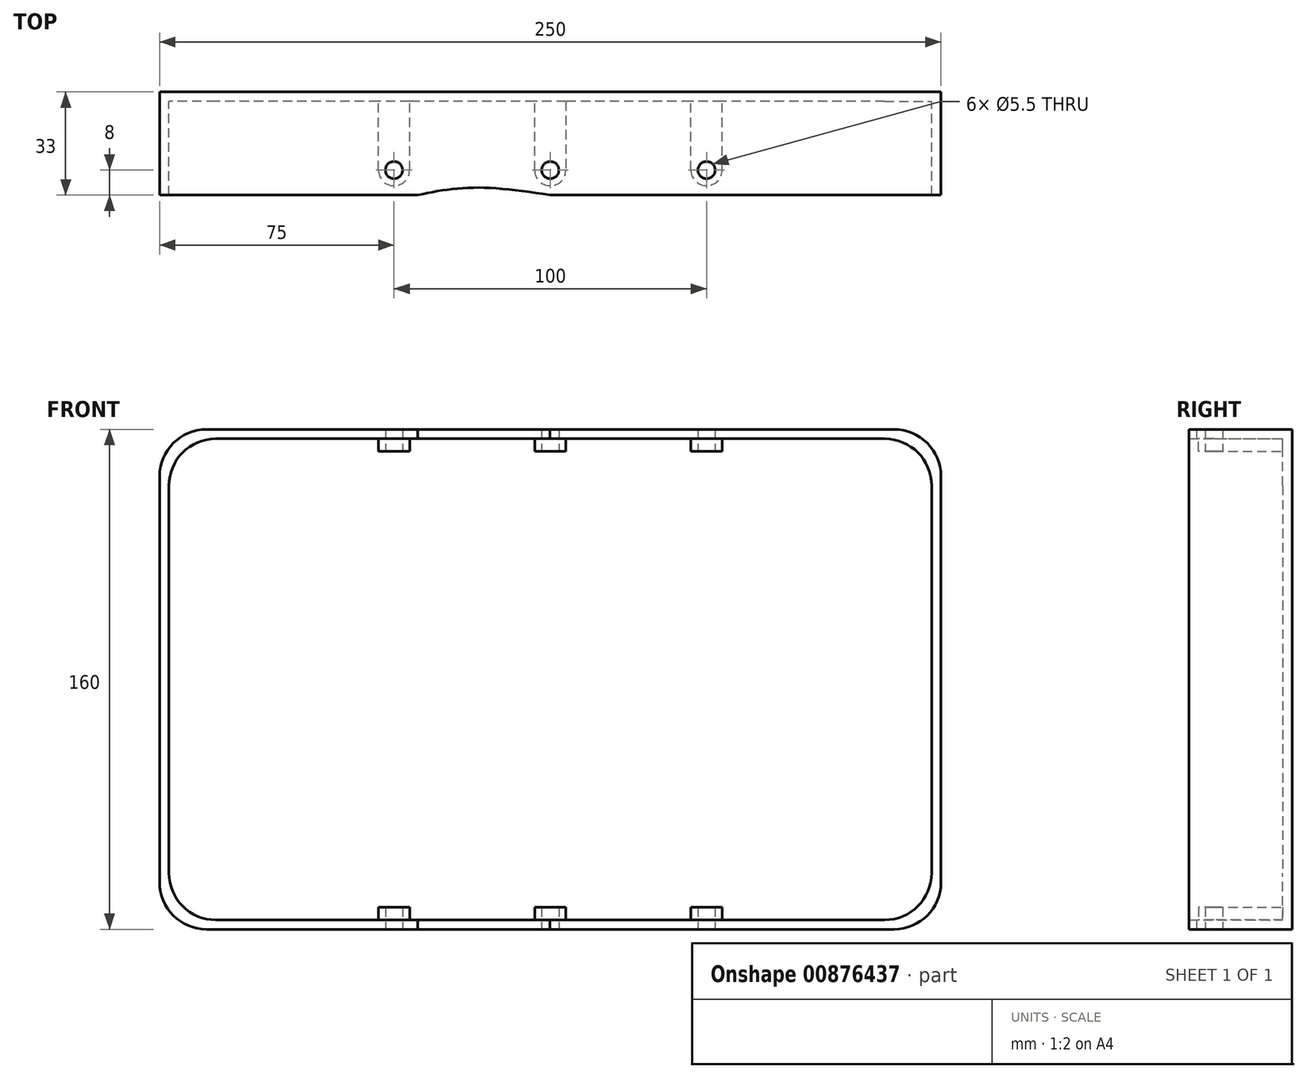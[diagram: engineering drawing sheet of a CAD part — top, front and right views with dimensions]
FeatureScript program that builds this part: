
annotation { "Feature Type Name" : "Feature", "Feature Type Description" : "" }
export const myFeature = defineFeature(function(context is Context, id is Id, definition is map)
    precondition{}
    {
        {
            var Q0;
            Q0=qCreatedBy(makeId("Front.planeOp"),FACE);
            var sketch = newSketch(context, id + "F0", { "sketchPlane" : qUnion([Q0])});
            skLineSegment(sketch, "E0.bottom", {"start": v(125, 80) * mm, "end": v(-125, 80) * mm});
            skLineSegment(sketch, "E0.top", {"start": v(125, -80) * mm, "end": v(-125, -80) * mm});
            skLineSegment(sketch, "E0.left", {"start": v(125, 80) * mm, "end": v(125, -80) * mm});
            skLineSegment(sketch, "E0.right", {"start": v(-125, 80) * mm, "end": v(-125, -80) * mm});
            skPoint(sketch, "E0.middle", {"position": v(0, 0) * mm});
            skSolve(sketch);
        }
        {
            var Q0;
            Q0 = qSketchRegion(id + "F0", true);
            extrude(context, id + "F1", {"entities" : qUnion([Q0]), "depth" : 3 * mm, "offsetDistance" : 25 * mm});
        }
        {
            var Q0;
            Q0=makeQuery(id+"F1.opExtrude","CAP_FACE",FACE,{"disambiguationData":[OSD([sQuery(id+"F0.wireOp",EDGE,"E0.bottom"),sQuery(id+"F0.wireOp",EDGE,"E0.top"),sQuery(id+"F0.wireOp",EDGE,"E0.left"),sQuery(id+"F0.wireOp",EDGE,"E0.right")])],"isStart":false});
            var sketch = newSketch(context, id + "F2", { "sketchPlane" : qUnion([Q0])});
            skLineSegment(sketch, "E1.0", {"start": v(125, 80) * mm, "end": v(-125, 80) * mm});
            skLineSegment(sketch, "E2.0", {"start": v(-125, 80) * mm, "end": v(-125, -80) * mm});
            skLineSegment(sketch, "E3.0", {"start": v(125, -80) * mm, "end": v(-125, -80) * mm});
            skLineSegment(sketch, "E4.0", {"start": v(125, 80) * mm, "end": v(125, -80) * mm});
            skLineSegment(sketch, "E5.0", {"start": v(122, 77) * mm, "end": v(-122, 77) * mm});
            skLineSegment(sketch, "E6.0", {"start": v(-122, 77) * mm, "end": v(-122, -77) * mm});
            skLineSegment(sketch, "E7.0", {"start": v(122, -77) * mm, "end": v(-122, -77) * mm});
            skLineSegment(sketch, "E8", {"start": v(122, 77) * mm, "end": v(122, -77) * mm});
            skSolve(sketch);
        }
        {
            var Q0;
            Q0=makeQuery(id+"F2.imprint","IMPRINT",FACE,{"disambiguationData":[TD([[makeQuery(id+"F2.imprint","IMPRINT",EDGE,{"derivedFrom":sQuery(id+"F2.wireOp",EDGE,"E1.0")}),1.0]])]});
            extrude(context, id + "F3", {"entities" : qUnion([Q0]), "operationType" : NewBodyOperationType.ADD, "depth" : 30 * mm, "offsetDistance" : 25 * mm});
        }
        {
            var Q0;
            Q0=makeQuery(id+"F3.boolean.opBoolean","MERGE",FACE,{"derivedFrom":[makeQuery(id+"F1.opExtrude","SWEPT_FACE",FACE,{"disambiguationData":[OSD([sQuery(id+"F0.wireOp",EDGE,"E0.top")])]}),makeQuery(id+"F3.opExtrude","SWEPT_FACE",FACE,{"disambiguationData":[OSD([sQuery(id+"F2.wireOp",EDGE,"E3.0")])]})]});
            var sketch = newSketch(context, id + "F4", { "sketchPlane" : qUnion([Q0])});
            skCircle(sketch, "E9", {"center": v(0, 25) * mm, "radius": 2.75 * mm});
            skCircle(sketch, "E10", {"center": v(-50, 25) * mm, "radius": 2.75 * mm});
            skCircle(sketch, "E11", {"center": v(50, 25) * mm, "radius": 2.75 * mm});
            skSolve(sketch);
        }
        {
            var Q0;
            Q0=makeQuery(id+"F4.imprint","IMPRINT",FACE,{"disambiguationData":[TD([[makeQuery(id+"F4.imprint","IMPRINT",EDGE,{"derivedFrom":sQuery(id+"F4.wireOp",EDGE,"E9")}),1.0]])]});
            var Q1;
            Q1=makeQuery(id+"F4.imprint","IMPRINT",FACE,{"disambiguationData":[TD([[makeQuery(id+"F4.imprint","IMPRINT",EDGE,{"derivedFrom":sQuery(id+"F4.wireOp",EDGE,"E10")}),1.0]])]});
            var Q2;
            Q2=makeQuery(id+"F4.imprint","IMPRINT",FACE,{"disambiguationData":[TD([[makeQuery(id+"F4.imprint","IMPRINT",EDGE,{"derivedFrom":sQuery(id+"F4.wireOp",EDGE,"E11")}),1.0]])]});
            extrude(context, id + "F5", {"entities" : qUnion([Q0, Q1, Q2]), "operationType" : NewBodyOperationType.REMOVE, "endBound" : BoundingType.THROUGH_ALL, "oppositeDirection" : true, "depth" : 25 * mm, "offsetDistance" : 25 * mm});
        }
        {
            var Q0;
            Q0=makeQuery(id+"F3.boolean.opBoolean","MERGE",EDGE,{"derivedFrom":[makeQuery(id+"F1.opExtrude","SWEPT_EDGE",EDGE,{"disambiguationData":[OSD([sQuery(id+"F0.wireOp",EDGE,"E0.top"),sQuery(id+"F0.wireOp",EDGE,"E0.right")])]}),makeQuery(id+"F3.opExtrude","SWEPT_EDGE",EDGE,{"disambiguationData":[OSD([sQuery(id+"F2.wireOp",EDGE,"E2.0"),sQuery(id+"F2.wireOp",EDGE,"E3.0")])]})]});
            var Q1;
            Q1=makeQuery(id+"F3.boolean.opBoolean","MERGE",EDGE,{"derivedFrom":[makeQuery(id+"F1.opExtrude","SWEPT_EDGE",EDGE,{"disambiguationData":[OSD([sQuery(id+"F0.wireOp",EDGE,"E0.bottom"),sQuery(id+"F0.wireOp",EDGE,"E0.right")])]}),makeQuery(id+"F3.opExtrude","SWEPT_EDGE",EDGE,{"disambiguationData":[OSD([sQuery(id+"F2.wireOp",EDGE,"E1.0"),sQuery(id+"F2.wireOp",EDGE,"E2.0")])]})]});
            var Q2;
            Q2=makeQuery(id+"F3.boolean.opBoolean","MERGE",EDGE,{"derivedFrom":[makeQuery(id+"F1.opExtrude","SWEPT_EDGE",EDGE,{"disambiguationData":[OSD([sQuery(id+"F0.wireOp",EDGE,"E0.bottom"),sQuery(id+"F0.wireOp",EDGE,"E0.left")])]}),makeQuery(id+"F3.opExtrude","SWEPT_EDGE",EDGE,{"disambiguationData":[OSD([sQuery(id+"F2.wireOp",EDGE,"E1.0"),sQuery(id+"F2.wireOp",EDGE,"E4.0")])]})]});
            var Q3;
            Q3=makeQuery(id+"F3.boolean.opBoolean","MERGE",EDGE,{"derivedFrom":[makeQuery(id+"F1.opExtrude","SWEPT_EDGE",EDGE,{"disambiguationData":[OSD([sQuery(id+"F0.wireOp",EDGE,"E0.top"),sQuery(id+"F0.wireOp",EDGE,"E0.left")])]}),makeQuery(id+"F3.opExtrude","SWEPT_EDGE",EDGE,{"disambiguationData":[OSD([sQuery(id+"F2.wireOp",EDGE,"E3.0"),sQuery(id+"F2.wireOp",EDGE,"E4.0")])]})]});
            var Q4;
            Q4=makeQuery(id+"F3.opExtrude","SWEPT_EDGE",EDGE,{"disambiguationData":[OSD([sQuery(id+"F2.wireOp",EDGE,"E5.0"),sQuery(id+"F2.wireOp",EDGE,"E8")])]});
            var Q5;
            Q5=makeQuery(id+"F3.opExtrude","SWEPT_EDGE",EDGE,{"disambiguationData":[OSD([sQuery(id+"F2.wireOp",EDGE,"E5.0"),sQuery(id+"F2.wireOp",EDGE,"E6.0")])]});
            var Q6;
            Q6=makeQuery(id+"F3.opExtrude","SWEPT_EDGE",EDGE,{"disambiguationData":[OSD([sQuery(id+"F2.wireOp",EDGE,"E6.0"),sQuery(id+"F2.wireOp",EDGE,"E7.0")])]});
            var Q7;
            Q7=makeQuery(id+"F3.opExtrude","SWEPT_EDGE",EDGE,{"disambiguationData":[OSD([sQuery(id+"F2.wireOp",EDGE,"E7.0"),sQuery(id+"F2.wireOp",EDGE,"E8")])]});
            fillet(context, id + "F6", {"entities" : qUnion([Q0, Q1, Q2, Q3, Q4, Q5, Q6, Q7]), "radius" : 15 * mm, "tangentPropagation" : true, "allowEdgeOverflow" : false});
        }
        {
            var Q0;
            Q0=makeQuery(id+"F4.imprint","IMPRINT",FACE,{"disambiguationData":[TD([[makeQuery(id+"F4.imprint","IMPRINT",EDGE,{"derivedFrom":sQuery(id+"F4.wireOp",EDGE,"E9")}),-1.0]])]});
            var sketch = newSketch(context, id + "F7", { "sketchPlane" : qUnion([Q0])});
            skFitSpline(sketch, "E12", {"points": [v(-161.6, 24.56) * mm, v(-113.27, 38.05) * mm, v(-54.94, 35.87) * mm, v(-21, 30.65) * mm, v(46.92, 38.49) * mm, v(123.53, 27.17) * mm, v(174.02, 33.26) * mm, v(165.32, 75.92) * mm, v(77.39, 101.17) * mm, v(70.42, 102.04) * mm, v(-44.93, 102.04) * mm, v(-113.27, 90.72) * mm, v(-179.44, 44.58) * mm, v(-161.6, 24.56) * mm]});
            skSolve(sketch);
        }
        {
            var Q0;
            {var subQ1=sQuery(id+"F2.wireOp",EDGE,"E3.0");var subQ7=makeQuery(id+"F4.imprint","IMPRINT",EDGE,{"derivedFrom":makeQuery(id+"F3.opExtrude","CAP_EDGE",EDGE,{"disambiguationData":[OSD([subQ1])],"isStart":false})});Q0=makeQuery(id+"F7.imprint","IMPRINT",FACE,{"disambiguationData":[TD([[makeQuery(id+"F7.imprint","IMPRINT",EDGE,{"derivedFrom":subQ7}),-1.0]])]});}
            var Q1;
            {var subQ1=sQuery(id+"F2.wireOp",EDGE,"E3.0");var subQ7=makeQuery(id+"F4.imprint","IMPRINT",EDGE,{"derivedFrom":makeQuery(id+"F3.opExtrude","CAP_EDGE",EDGE,{"disambiguationData":[OSD([subQ1])],"isStart":false})});Q1=makeQuery(id+"F7.imprint","IMPRINT",FACE,{"disambiguationData":[TD([[makeQuery(id+"F7.imprint","IMPRINT",EDGE,{"derivedFrom":subQ7}),1.0]])]});}
            extrude(context, id + "F8", {"entities" : qUnion([Q0, Q1]), "operationType" : NewBodyOperationType.REMOVE, "endBound" : BoundingType.THROUGH_ALL, "oppositeDirection" : true, "depth" : 25 * mm, "offsetDistance" : 25 * mm});
        }
        {
            var Q0;
            Q0=makeQuery(id+"F3.opExtrude","SWEPT_FACE",FACE,{"disambiguationData":[OSD([sQuery(id+"F2.wireOp",EDGE,"E5.0")])]});
            var sketch = newSketch(context, id + "F9", { "sketchPlane" : qUnion([Q0])});
            skArc(sketch, "E13", {"start": v(-45, 25) * mm, "mid": v(-50, 30) * mm, "end": v(-55, 25) * mm});
            skArc(sketch, "E14", {"start": v(5, 25) * mm, "mid": v(0, 30) * mm, "end": v(-5, 25) * mm});
            skArc(sketch, "E15", {"start": v(55, 25) * mm, "mid": v(50, 30) * mm, "end": v(45, 25) * mm});
            skCircle(sketch, "E16.0", {"center": v(0, 25) * mm, "radius": 2.75 * mm});
            skCircle(sketch, "E17.0", {"center": v(50, 25) * mm, "radius": 2.75 * mm});
            skCircle(sketch, "E18.0", {"center": v(-50, 25) * mm, "radius": 2.75 * mm});
            skLineSegment(sketch, "E19", {"start": v(-45, 25) * mm, "end": v(-45, 3) * mm});
            skLineSegment(sketch, "E20", {"start": v(-55, 25) * mm, "end": v(-55, 3) * mm});
            skLineSegment(sketch, "E21", {"start": v(-55, 3) * mm, "end": v(-45, 3) * mm});
            skLineSegment(sketch, "E22", {"start": v(-45, 3) * mm, "end": v(-55, 3) * mm});
            skLineSegment(sketch, "E23", {"start": v(-5, 25.08) * mm, "end": v(-5, 3) * mm});
            skLineSegment(sketch, "E24", {"start": v(-5, 3) * mm, "end": v(5, 3) * mm});
            skLineSegment(sketch, "E25", {"start": v(5, 3) * mm, "end": v(5, 25) * mm});
            skLineSegment(sketch, "E26", {"start": v(45, 25) * mm, "end": v(45, 3) * mm});
            skLineSegment(sketch, "E27", {"start": v(55, 25.08) * mm, "end": v(55, 3) * mm});
            skLineSegment(sketch, "E28", {"start": v(55, 3) * mm, "end": v(45, 3) * mm});
            skSolve(sketch);
        }
        {
            var Q0;
            Q0 = qSketchRegion(id + "F9", true);
            extrude(context, id + "F10", {"entities" : qUnion([Q0]), "operationType" : NewBodyOperationType.ADD, "depth" : 4 * mm, "offsetDistance" : 25 * mm});
        }
        {
            var Q0;
            Q0=makeQuery(id+"F3.opExtrude","SWEPT_FACE",FACE,{"disambiguationData":[OSD([sQuery(id+"F2.wireOp",EDGE,"E7.0")])]});
            var sketch = newSketch(context, id + "F11", { "sketchPlane" : qUnion([Q0])});
            skArc(sketch, "E29.0", {"start": v(-45, -25) * mm, "mid": v(-50, -30) * mm, "end": v(-55, -25) * mm});
            skLineSegment(sketch, "E30.0", {"start": v(-55, -25) * mm, "end": v(-55, -3) * mm});
            skLineSegment(sketch, "E31.0", {"start": v(-45, -25) * mm, "end": v(-45, -3) * mm});
            skLineSegment(sketch, "E32.0", {"start": v(-45, -3) * mm, "end": v(-55, -3) * mm});
            skLineSegment(sketch, "E33.0.2", {"start": v(-55, -3) * mm, "end": v(-45, -3) * mm});
            skLineSegment(sketch, "E33.0.3", {"start": v(-45, -3) * mm, "end": v(-45, -25) * mm});
            skLineSegment(sketch, "E34.0.0", {"start": v(-5, -3) * mm, "end": v(5, -3) * mm});
            skLineSegment(sketch, "E34.0.1", {"start": v(5, -3) * mm, "end": v(5, -25) * mm});
            skArc(sketch, "E34.0.2", {"start": v(5, -25) * mm, "mid": v(0, -30) * mm, "end": v(-5, -25) * mm});
            skLineSegment(sketch, "E34.0.3", {"start": v(-5, -25) * mm, "end": v(-5, -3) * mm});
            skLineSegment(sketch, "E35.0.0", {"start": v(55, -3) * mm, "end": v(55, -25) * mm});
            skArc(sketch, "E35.0.1", {"start": v(55, -25) * mm, "mid": v(50, -30) * mm, "end": v(45, -25) * mm});
            skLineSegment(sketch, "E35.0.2", {"start": v(45, -25) * mm, "end": v(45, -3) * mm});
            skLineSegment(sketch, "E35.0.3", {"start": v(45, -3) * mm, "end": v(55, -3) * mm});
            skCircle(sketch, "E36.0", {"center": v(-50, -25) * mm, "radius": 2.75 * mm});
            skCircle(sketch, "E37.0", {"center": v(0, -25) * mm, "radius": 2.75 * mm});
            skCircle(sketch, "E37.1", {"center": v(50, -25) * mm, "radius": 2.75 * mm});
            skSolve(sketch);
        }
        {
            var Q0;
            Q0 = qSketchRegion(id + "F11", true);
            extrude(context, id + "F12", {"entities" : qUnion([Q0]), "operationType" : NewBodyOperationType.ADD, "depth" : 4 * mm, "offsetDistance" : 25 * mm});
        }
    });
